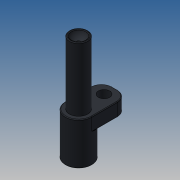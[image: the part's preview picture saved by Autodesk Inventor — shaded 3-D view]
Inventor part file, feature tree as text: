
AUTODESK INVENTOR PART (.ipt)
format: ipt  version: 2018.3 (Build 223284000, 284)  size: 221,184 bytes
history: native  units: in
note: dims shown in document units (in); Inventor stores cm internally (conversion verified against a paired STEP export)
features: hole x3, sketch x2, fillet x2, revolve x1, extrude x1
ambient origin geometry x8: Origin, YZ Plane, XZ Plane, XY Plane, X Axis, Y Axis, Z Axis, Center Point
bodies: Solid1 (feature_tree)
feature tree (9):
  revolve  "Revolution1"  [1 undecoded]
  sketch  "Sketch2"  dims[d2=0.4331in d3=0.625in d4=1.0in d5=1.5in d6=90.0deg d7=0.05in d8=0.75in d9=0.375in d10=0.25in d11=0.5635in d12=1.0in d13=0.8108in d14=0.313in d15=0.273in d16=0.0246in d17=0.327in d18=0.375in d19=0.25in d20=0.5635in d21=0.6in d22=0.8108in d24=0.32in d25=0.0in d34=0.25in d35=0.016in d36=0.85in d39=0.25in d40=0.266in d41=0.75in d42=0.438in d43=0.25in d44=0.5635in d45=1.0in d46=0.8108in]
  hole  "Hole1"  [1 undecoded]
  hole  "Hole2"  [1 undecoded]
  extrude  "Extrusion1"  Depth=1.5in
  hole  "Hole4"  [1 undecoded]
  fillet  "Fillet1"  Radius=0.32in
  fillet  "Fillet2"  Radius=0.25in
  sketch  "Sketch1"  dims[d0=0.3563in d1=0.0394in]
note: 4 required parameter values undecoded (feature->parameter linkage not recoverable at this tier; creation-order binding heuristic only, values carry confidence <= 0.55)